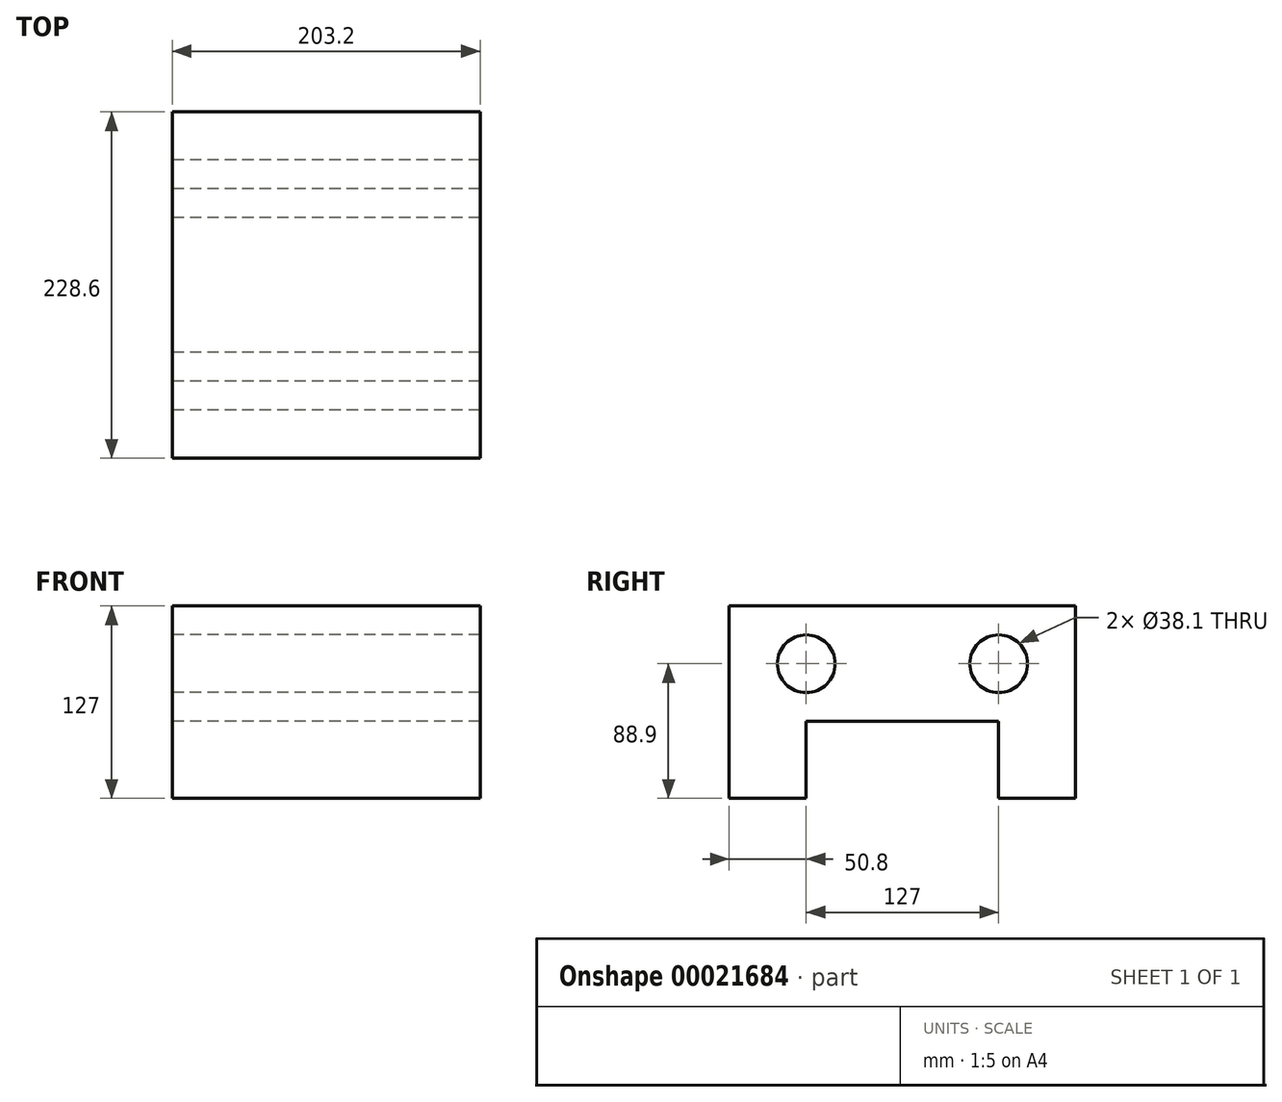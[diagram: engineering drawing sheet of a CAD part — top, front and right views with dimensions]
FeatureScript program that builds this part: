
annotation { "Feature Type Name" : "Feature", "Feature Type Description" : "" }
export const myFeature = defineFeature(function(context is Context, id is Id, definition is map)
    precondition{}
    {
        {
            var Q0;
            Q0=qCreatedBy(makeId("Right.planeOp"),FACE);
            var sketch = newSketch(context, id + "F0", { "sketchPlane" : qUnion([Q0])});
            skLineSegment(sketch, "E0.rect.bottom", {"start": v(114.3, 63.5) * mm, "end": v(-114.3, 63.5) * mm});
            skLineSegment(sketch, "E0.rect.left", {"start": v(114.3, 63.5) * mm, "end": v(114.3, -63.5) * mm});
            skLineSegment(sketch, "E0.rect.right", {"start": v(-114.3, 63.5) * mm, "end": v(-114.3, -63.5) * mm});
            skPoint(sketch, "E0.rect.middle", {"position": v(0, 0) * mm});
            skLineSegment(sketch, "E1", {"start": v(-114.3, -63.5) * mm, "end": v(-63.5, -63.5) * mm});
            skLineSegment(sketch, "E2", {"start": v(-63.5, -63.5) * mm, "end": v(-63.5, -12.7) * mm});
            skLineSegment(sketch, "E3", {"start": v(-63.5, -12.7) * mm, "end": v(63.5, -12.7) * mm});
            skLineSegment(sketch, "E4", {"start": v(63.5, -12.7) * mm, "end": v(63.5, -63.5) * mm});
            skLineSegment(sketch, "E5", {"start": v(63.5, -63.5) * mm, "end": v(114.3, -63.5) * mm});
            skCircle(sketch, "E6", {"center": v(-63.5, 25.4) * mm, "radius": 19.05 * mm});
            skCircle(sketch, "E7", {"center": v(63.5, 25.4) * mm, "radius": 19.05 * mm});
            skLineSegment(sketch, "E8", {"start": v(-63.5, 25.4) * mm, "end": v(-114.3, 25.4) * mm, "construction": true});
            skLineSegment(sketch, "E9", {"start": v(-63.5, 25.4) * mm, "end": v(114.3, 25.4) * mm, "construction": true});
            skSolve(sketch);
        }
        {
            var Q0;
            Q0 = qSketchRegion(id + "F0", true);
            extrude(context, id + "F1", {"entities" : qUnion([Q0]), "depth" : 203.2 * mm});
        }
    });
